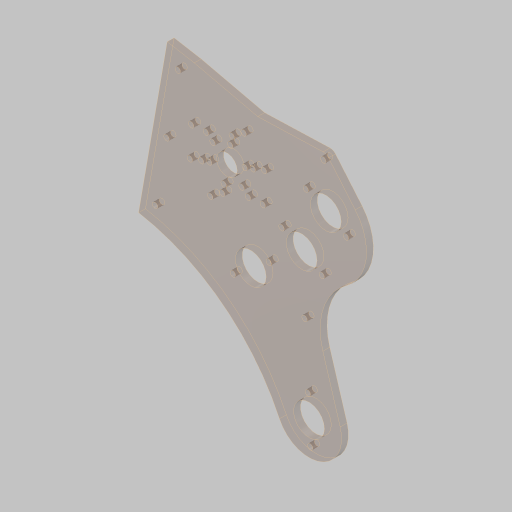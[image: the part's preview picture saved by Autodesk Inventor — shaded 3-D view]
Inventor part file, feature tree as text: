
AUTODESK INVENTOR PART (.ipt)
format: ipt  version: 2023.5 (Build 275446000, 446)  size: 327,680 bytes
history: native  units: in
note: dims shown in document units (in); Inventor stores cm internally (conversion verified against a paired STEP export)
features: sketch x4, hole x3, extrude x2, projected_geometry x2
ambient origin geometry x8: Origin, YZ Plane, XZ Plane, XY Plane, X Axis, Y Axis, Z Axis, Center Point
bodies: Solid1 (feature_tree)
feature tree (11):
  sketch  "Sketch1"  dims[d3=45.0deg d4=0.0in]
  extrude  "Extrusion1"  TaperAngle=0.0deg  [1 undecoded]
  hole  "Hole1"  [1 undecoded]
  hole  "Hole2"  [1 undecoded]
  extrude  "Extrusion2"  Depth=1.75in
  hole  "Hole3"  [1 undecoded]
  sketch  "Sketch2"  dims[d7=4.0in d8=4.0in]
  projected_geometry  "Projected Loop1"
  sketch  "Sketch3"  dims[d9=1.123in d10=4.0in]
  projected_geometry  "Projected Loop2"
  sketch  "Sketch4"  dims[d11=4.5in d12=4.5in d13=0.625in d14=0.625in d15=5.181in d16=1.128in d17=5.181in d18=1.8765in d19=1.8765in d22=1.0in d23=6.0in d26=10.5532in d27=2.5in d30=8.0in d31=0.0687in d32=0.75in d33=4.75in d34=1.375in d35=0.75in d36=0.25in d38=2.3622in d40=360.0deg d44=0.375in d45=0.25in d46=0.0in d47=0.201in d48=0.75in d49=0.37in d50=0.25in d51=90.0deg d52=1.0in d53=0.8108in d55=0.5497in d56=0.3in d57=0.25in d58=2.256in d59=2.5in d60=2.9555in d61=2.35in d62=0.3779in d65=2.0in d66=2.3622in d68=360.0deg d70=1.625in d71=60.0deg d72=1.655in d73=0.201in d74=0.75in d75=0.385in d76=0.25in d77=0.5635in d78=1.0in d79=0.8108in d80=1.5748in d82=360.0deg d85=1.5748in d87=360.0deg d89=45.0deg d90=4.0in d91=1.125in d92=0.625in d93=5.181in d94=0.0in d95=5.5in d96=8.0in d99=0.3126in d100=15.9834in d101=4.0in d102=0.375in d103=5.75in d104=0.375in d105=1.64in d106=1.64in d108=1.6875in d109=0.375in d110=1.4304in d111=0.5in d112=15.0deg d113=1.0in d114=0.0in d115=0.201in d116=0.75in d117=0.385in d118=0.25in d119=0.5635in d120=1.0in d121=0.8108in d122=1.75in]
note: 4 required parameter values undecoded (feature->parameter linkage not recoverable at this tier; creation-order binding heuristic only, values carry confidence <= 0.55)
